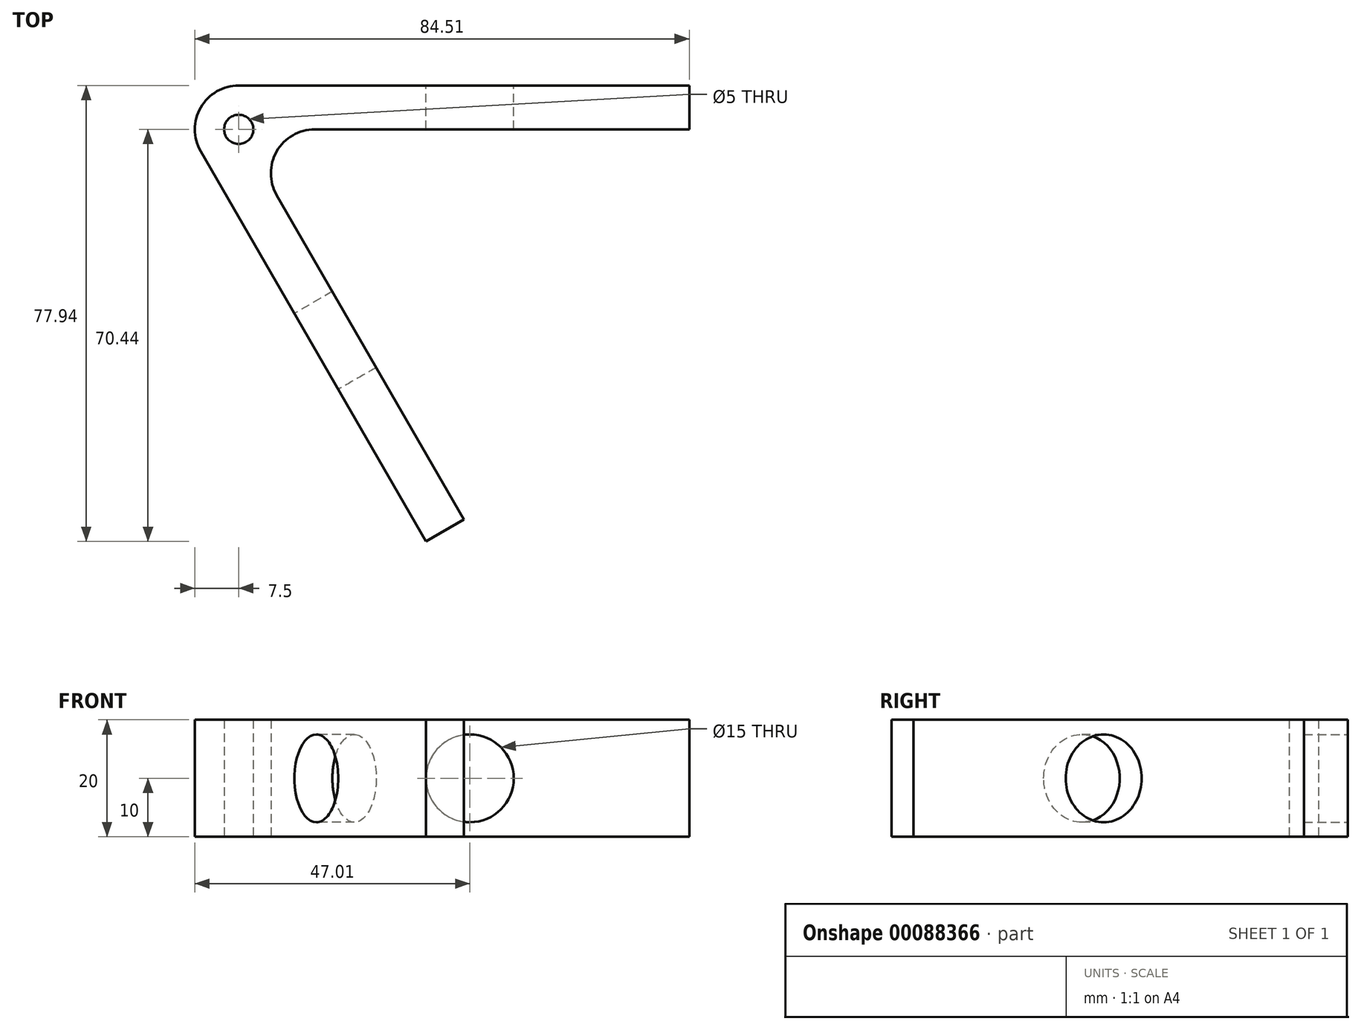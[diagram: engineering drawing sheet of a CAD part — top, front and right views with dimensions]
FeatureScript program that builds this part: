
annotation { "Feature Type Name" : "Feature", "Feature Type Description" : "" }
export const myFeature = defineFeature(function(context is Context, id is Id, definition is map)
    precondition{}
    {
        {
            var Q0;
            Q0=qCreatedBy(makeId("Top.planeOp"),FACE);
            var sketch = newSketch(context, id + "F0", { "sketchPlane" : qUnion([Q0])});
            skLineSegment(sketch, "E0", {"start": v(13, 0) * mm, "end": v(90, 0) * mm});
            skLineSegment(sketch, "E1", {"start": v(0, 0) * mm, "end": v(47.25, -27.28) * mm, "construction": true});
            skLineSegment(sketch, "E2.MirrorCS", {"start": v(6.5, -11.25) * mm, "end": v(45, -77.94) * mm});
            skPoint(sketch, "E3.visualSharp", {"position": v(0, 0) * mm});
            skArc(sketch, "E3.filletArc", {"start": v(13, 0) * mm, "mid": v(6.5, -3.75) * mm, "end": v(6.5, -11.25) * mm});
            skLineSegment(sketch, "E4", {"start": v(90, 0) * mm, "end": v(90, -7.5) * mm});
            skLineSegment(sketch, "E5", {"start": v(90, -7.5) * mm, "end": v(25.98, -7.5) * mm});
            skLineSegment(sketch, "E6", {"start": v(19.49, -18.75) * mm, "end": v(51.5, -74.2) * mm});
            skLineSegment(sketch, "E7", {"start": v(51.5, -74.2) * mm, "end": v(45, -77.94) * mm});
            skArc(sketch, "E8.filletArc", {"start": v(25.98, -7.5) * mm, "mid": v(19.49, -11.25) * mm, "end": v(19.49, -18.75) * mm});
            skLineSegment(sketch, "E9", {"start": v(6.5, -3.75) * mm, "end": v(19.49, -11.25) * mm, "construction": true});
            skCircle(sketch, "E10", {"center": v(13, -7.5) * mm, "radius": 2.5 * mm});
            skSolve(sketch);
        }
        {
            var Q0;
            Q0 = qSketchRegion(id + "F0", true);
            extrude(context, id + "F1", {"entities" : qUnion([Q0]), "depth" : 20 * mm});
        }
        {
            var Q0;
            Q0=makeQuery(id+"F1.opExtrude","SWEPT_FACE",FACE,{"disambiguationData":[OSD([sQuery(id+"F0.wireOp",EDGE,"E2.MirrorCS")])]});
            var sketch = newSketch(context, id + "F2", { "sketchPlane" : qUnion([Q0])});
            skLineSegment(sketch, "E11", {"start": v(90, 10) * mm, "end": v(60, 10) * mm, "construction": true});
            skCircle(sketch, "E12", {"center": v(52.5, 10) * mm, "radius": 7.5 * mm});
            skSolve(sketch);
        }
        {
            var Q0;
            Q0 = qSketchRegion(id + "F2", true);
            extrude(context, id + "F3", {"entities" : qUnion([Q0]), "operationType" : NewBodyOperationType.REMOVE, "oppositeDirection" : true, "depth" : 25 * mm});
        }
        {
            var Q0;
            Q0=makeQuery(id+"F1.opExtrude","SWEPT_FACE",FACE,{"disambiguationData":[OSD([sQuery(id+"F0.wireOp",EDGE,"E0")])]});
            var sketch = newSketch(context, id + "F4", { "sketchPlane" : qUnion([Q0])});
            skLineSegment(sketch, "E13", {"start": v(-90, 10) * mm, "end": v(-60, 10) * mm, "construction": true});
            skCircle(sketch, "E14", {"center": v(-52.5, 10) * mm, "radius": 7.5 * mm});
            skSolve(sketch);
        }
        {
            var Q0;
            Q0 = qSketchRegion(id + "F4", true);
            extrude(context, id + "F5", {"entities" : qUnion([Q0]), "operationType" : NewBodyOperationType.REMOVE, "oppositeDirection" : true, "depth" : 25 * mm});
        }
    });
